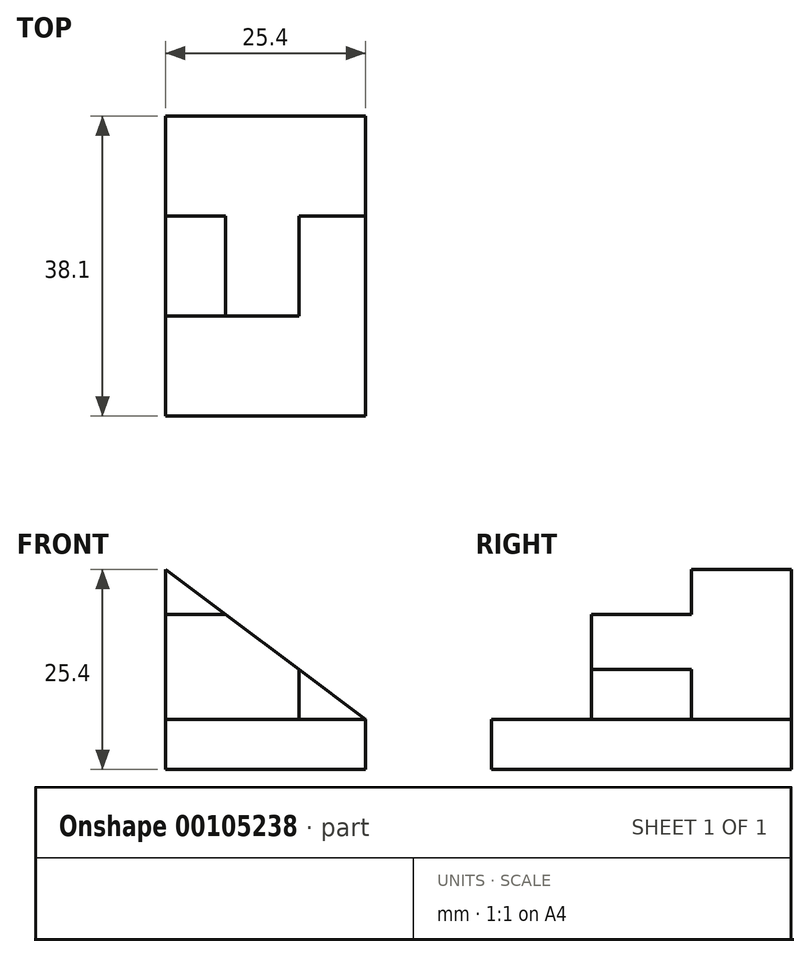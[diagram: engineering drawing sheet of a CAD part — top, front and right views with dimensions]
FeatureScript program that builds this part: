
annotation { "Feature Type Name" : "Feature", "Feature Type Description" : "" }
export const myFeature = defineFeature(function(context is Context, id is Id, definition is map)
    precondition{}
    {
        {
            var Q0;
            Q0=qCreatedBy(makeId("Front.planeOp"),FACE);
            var sketch = newSketch(context, id + "F0", { "sketchPlane" : qUnion([Q0])});
            skLineSegment(sketch, "E0", {"start": v(0, 0) * mm, "end": v(25.4, 0) * mm});
            skLineSegment(sketch, "E1", {"start": v(25.4, 0) * mm, "end": v(25.4, 6.35) * mm});
            skLineSegment(sketch, "E2", {"start": v(25.4, 6.35) * mm, "end": v(0, 6.35) * mm});
            skLineSegment(sketch, "E3", {"start": v(0, 6.35) * mm, "end": v(0, 0) * mm});
            skSolve(sketch);
        }
        {
            var Q0;
            Q0 = qSketchRegion(id + "F0", true);
            extrude(context, id + "F1", {"entities" : qUnion([Q0]), "depth" : 38.1 * mm});
        }
        {
            var Q0;
            Q0=qCreatedBy(makeId("Front.planeOp"),FACE);
            var sketch = newSketch(context, id + "F2", { "sketchPlane" : qUnion([Q0])});
            skLineSegment(sketch, "E4", {"start": v(25.4, 6.35) * mm, "end": v(0, 6.35) * mm});
            skLineSegment(sketch, "E5", {"start": v(0, 6.35) * mm, "end": v(0, 25.4) * mm});
            skLineSegment(sketch, "E6", {"start": v(0, 25.4) * mm, "end": v(25.4, 6.35) * mm});
            skSolve(sketch);
        }
        {
            var Q0;
            Q0 = qSketchRegion(id + "F2", true);
            extrude(context, id + "F3", {"entities" : qUnion([Q0]), "operationType" : NewBodyOperationType.ADD, "depth" : 12.7 * mm});
        }
        {
            var Q0;
            Q0=makeQuery(id+"F3.opExtrude","CAP_FACE",FACE,{"disambiguationData":[OSD([sQuery(id+"F2.wireOp",EDGE,"E4"),sQuery(id+"F2.wireOp",EDGE,"E5"),sQuery(id+"F2.wireOp",EDGE,"E6")])],"isStart":false});
            var sketch = newSketch(context, id + "F4", { "sketchPlane" : qUnion([Q0])});
            skLineSegment(sketch, "E7", {"start": v(0, 6.35) * mm, "end": v(0, 19.68) * mm});
            skLineSegment(sketch, "E8", {"start": v(0, 19.68) * mm, "end": v(7.62, 19.68) * mm});
            skLineSegment(sketch, "E9", {"start": v(7.62, 19.68) * mm, "end": v(16.93, 12.7) * mm});
            skLineSegment(sketch, "E10", {"start": v(16.93, 12.7) * mm, "end": v(16.93, 6.35) * mm});
            skLineSegment(sketch, "E11", {"start": v(16.93, 6.35) * mm, "end": v(0, 6.35) * mm});
            skSolve(sketch);
        }
        {
            var Q0;
            Q0 = qSketchRegion(id + "F4", true);
            extrude(context, id + "F5", {"entities" : qUnion([Q0]), "operationType" : NewBodyOperationType.ADD, "depth" : 12.7 * mm});
        }
    });
